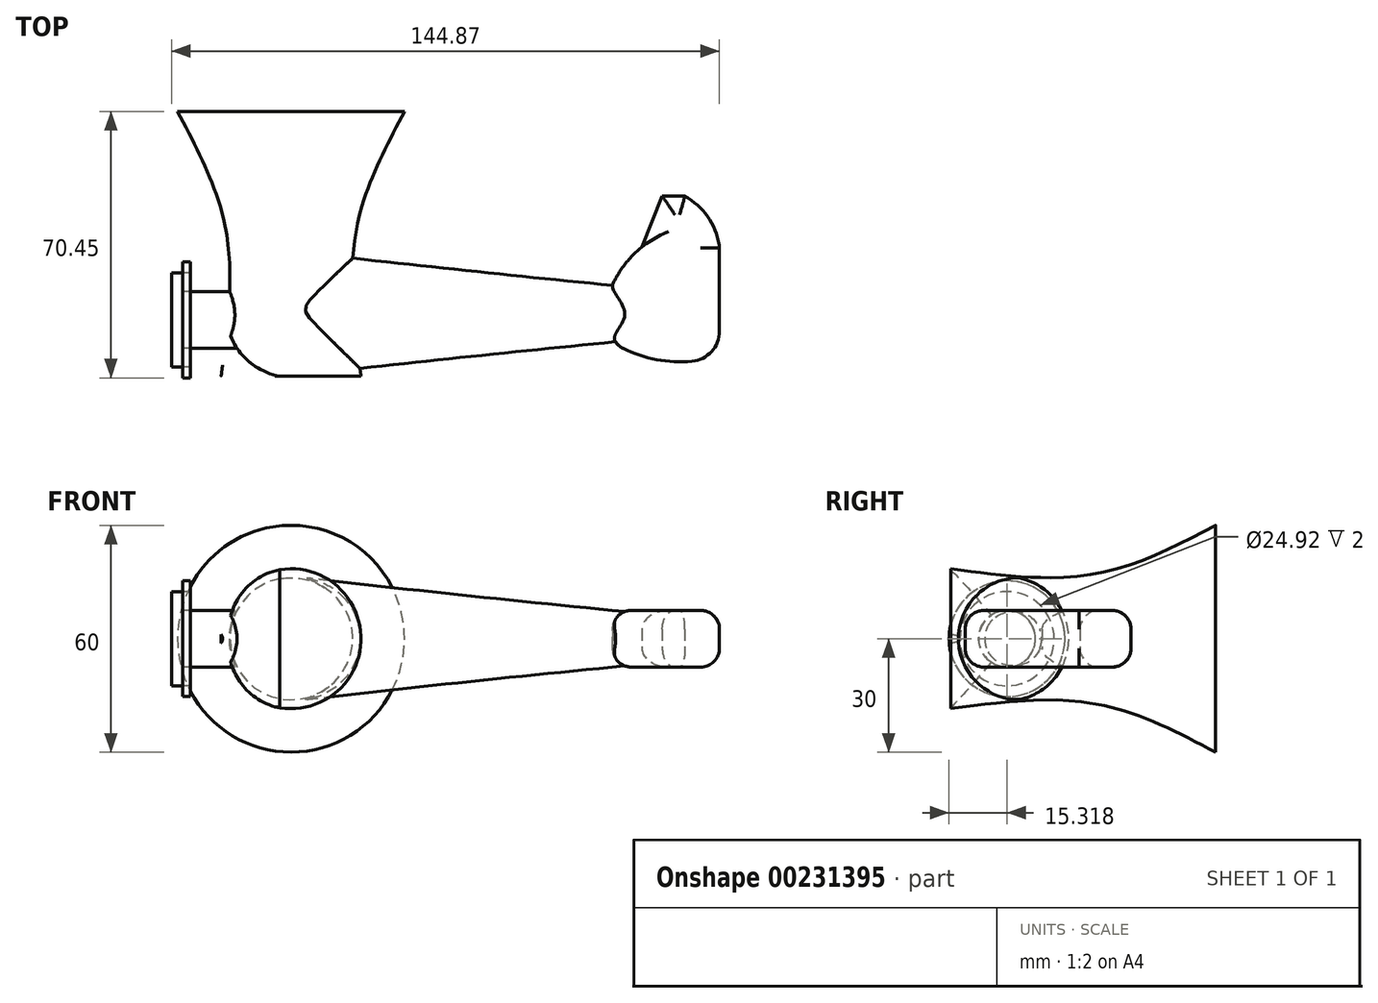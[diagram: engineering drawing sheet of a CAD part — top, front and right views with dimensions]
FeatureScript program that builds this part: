
annotation { "Feature Type Name" : "Feature", "Feature Type Description" : "" }
export const myFeature = defineFeature(function(context is Context, id is Id, definition is map)
    precondition{}
    {
        {
            var Q0;
            Q0=qCreatedBy(makeId("Front.planeOp"),FACE);
            var sketch = newSketch(context, id + "F0", { "sketchPlane" : qUnion([Q0])});
            skCircle(sketch, "E0", {"center": v(0, 0) * mm, "radius": 30 * mm});
            skSolve(sketch);
        }
        {
            var Q0;
            Q0=makeQuery(id+"F0.imprint","IMPRINT",FACE,{"disambiguationData":[TD([[makeQuery(id+"F0.imprint","IMPRINT",EDGE,{"derivedFrom":sQuery(id+"F0.wireOp",EDGE,"E0")}),1.0]])]});
            cPlane(context, id + "F1", {"entities" : qUnion([Q0]), "cplaneType" : CPlaneType.OFFSET, "offset" : 70 * mm, "width" : 150 * mm, "height" : 150 * mm});
        }
        {
            var Q0;
            Q0=qCreatedBy(id+"F1.planeOp",FACE);
            cPlane(context, id + "F2", {"entities" : qUnion([Q0]), "cplaneType" : CPlaneType.OFFSET, "offset" : 40 * mm, "oppositeDirection" : true, "width" : 150 * mm, "height" : 150 * mm});
        }
        {
            var Q0;
            Q0=qCreatedBy(id+"F2.planeOp",FACE);
            var sketch = newSketch(context, id + "F3", { "sketchPlane" : qUnion([Q0])});
            skCircle(sketch, "E1", {"center": v(0, 0) * mm, "radius": 17.5 * mm});
            skSolve(sketch);
        }
        {
            var Q0;
            Q0=qCreatedBy(id+"F1.planeOp",FACE);
            var sketch = newSketch(context, id + "F4", { "sketchPlane" : qUnion([Q0])});
            skCircle(sketch, "E2", {"center": v(0, 0) * mm, "radius": 18.5 * mm});
            skSolve(sketch);
        }
        {
            var Q0;
            Q0=makeQuery(id+"F4.imprint","IMPRINT",FACE,{"disambiguationData":[TD([[makeQuery(id+"F4.imprint","IMPRINT",EDGE,{"derivedFrom":sQuery(id+"F4.wireOp",EDGE,"E2")}),1.0]])]});
            var Q1;
            Q1=makeQuery(id+"F3.imprint","IMPRINT",FACE,{"disambiguationData":[TD([[makeQuery(id+"F3.imprint","IMPRINT",EDGE,{"derivedFrom":sQuery(id+"F3.wireOp",EDGE,"E1")}),1.0]])]});
            var Q2;
            Q2=makeQuery(id+"F0.imprint","IMPRINT",FACE,{"disambiguationData":[TD([[makeQuery(id+"F0.imprint","IMPRINT",EDGE,{"derivedFrom":sQuery(id+"F0.wireOp",EDGE,"E0")}),1.0]])]});
            loft(context, id + "F5", {"sheetProfilesArray" : [{ "sheetProfileEntities" : qUnion([Q0]) }, { "sheetProfileEntities" : qUnion([Q1]) }, { "sheetProfileEntities" : qUnion([Q2]) }]});
        }
        {
            var Q0;
            Q0=qCreatedBy(makeId("Right.planeOp"),FACE);
            cPlane(context, id + "F6", {"entities" : qUnion([Q0]), "cplaneType" : CPlaneType.OFFSET, "offset" : 60 * mm, "width" : 150 * mm, "height" : 150 * mm});
        }
        {
            var Q0;
            Q0=qCreatedBy(id+"F6.planeOp",FACE);
            cPlane(context, id + "F7", {"entities" : qUnion([Q0]), "cplaneType" : CPlaneType.OFFSET, "offset" : 25 * mm, "width" : 150 * mm, "height" : 150 * mm});
        }
        {
            var Q0;
            Q0=qCreatedBy(makeId("Right.planeOp"),FACE);
            var sketch = newSketch(context, id + "F8", { "sketchPlane" : qUnion([Q0])});
            skCircle(sketch, "E3", {"center": v(-53.5, 0) * mm, "radius": 16.5 * mm});
            skSolve(sketch);
        }
        {
            var Q0;
            Q0=qCreatedBy(id+"F6.planeOp",FACE);
            var sketch = newSketch(context, id + "F9", { "sketchPlane" : qUnion([Q0])});
            skCircle(sketch, "E4", {"center": v(-53.5, 0) * mm, "radius": 10 * mm});
            skSolve(sketch);
        }
        {
            var Q0;
            Q0=qCreatedBy(id+"F7.planeOp",FACE);
            var sketch = newSketch(context, id + "F10", { "sketchPlane" : qUnion([Q0])});
            skCircle(sketch, "E5", {"center": v(-53.5, 0) * mm, "radius": 7.5 * mm});
            skSolve(sketch);
        }
        {
            var Q1;
            Q1=qSketchRegion(id+"F8",true);
            var Q2;
            Q2=qSketchRegion(id+"F9",true);
            var Q3;
            Q3=qSketchRegion(id+"F10",true);
            loft(context, id + "F11", {"operationType" : NewBodyOperationType.ADD, "sheetProfilesArray" : [{ "sheetProfileEntities" : qUnion([Q1]) }, { "sheetProfileEntities" : qUnion([Q2]) }, { "sheetProfileEntities" : qUnion([Q3]) }]});
        }
        {
            var Q0;
            Q0=qCreatedBy(makeId("Top.planeOp"),FACE);
            var sketch = newSketch(context, id + "F12", { "sketchPlane" : qUnion([Q0])});
            skArc(sketch, "E6", {"start": v(-2.52, -70.07) * mm, "mid": v(-11.8, -65.57) * mm, "end": v(-16.82, -56.57) * mm});
            skLineSegment(sketch, "E7", {"start": v(-2.52, -70.07) * mm, "end": v(-18.47, -70.07) * mm});
            skLineSegment(sketch, "E8", {"start": v(-18.47, -70.07) * mm, "end": v(-16.82, -56.57) * mm});
            skSolve(sketch);
        }
        {
            var Q0;
            Q0=qCreatedBy(makeId("Top.planeOp"),FACE);
            cPlane(context, id + "F13", {"entities" : qUnion([Q0]), "cplaneType" : CPlaneType.OFFSET, "offset" : 18 * mm, "oppositeDirection" : true, "width" : 150 * mm, "height" : 150 * mm});
        }
        {
            var Q0;
            Q0=qCreatedBy(makeId("Top.planeOp"),FACE);
            var sketch = newSketch(context, id + "F14", { "sketchPlane" : qUnion([Q0])});
            skArc(sketch, "E9.0", {"start": v(-2.52, -70.07) * mm, "mid": v(-11.8, -65.57) * mm, "end": v(-16.82, -56.57) * mm});
            skLineSegment(sketch, "E10.0", {"start": v(-2.52, -70.07) * mm, "end": v(-18.47, -70.07) * mm});
            skLineSegment(sketch, "E11.0", {"start": v(-18.47, -70.07) * mm, "end": v(-16.82, -56.57) * mm});
            skSolve(sketch);
        }
        {
            var Q0;
            Q0=qCreatedBy(id+"F13.planeOp",FACE);
            var sketch = newSketch(context, id + "F15", { "sketchPlane" : qUnion([Q0])});
            skArc(sketch, "E12.0", {"start": v(-2.52, -70.07) * mm, "mid": v(-11.8, -65.57) * mm, "end": v(-16.82, -56.57) * mm});
            skLineSegment(sketch, "E13.0", {"start": v(-2.52, -70.07) * mm, "end": v(-18.47, -70.07) * mm});
            skLineSegment(sketch, "E13.1", {"start": v(-18.47, -70.07) * mm, "end": v(-16.82, -56.57) * mm});
            skSolve(sketch);
        }
        {
            var Q0;
            Q0=qSketchRegion(id+"F15",true);
            extrude(context, id + "F16", {"entities" : qUnion([Q0]), "operationType" : NewBodyOperationType.REMOVE, "endBound" : BoundingType.THROUGH_ALL, "depth" : 25 * mm});
        }
        {
            var Q0;
            Q0=qCreatedBy(makeId("Top.planeOp"),FACE);
            var sketch = newSketch(context, id + "F17", { "sketchPlane" : qUnion([Q0])});
            skLineSegment(sketch, "E14", {"start": v(113.26, -61.15) * mm, "end": v(113.26, -35.74) * mm});
            skLineSegment(sketch, "E15", {"start": v(98.14, -22.36) * mm, "end": v(92.74, -35.88) * mm});
            skArc(sketch, "E16", {"start": v(113.26, -64.6) * mm, "mid": v(98.75, -65.96) * mm, "end": v(85, -61.15) * mm});
            skLineSegment(sketch, "E17", {"start": v(113.26, -64.6) * mm, "end": v(113.26, -61.15) * mm});
            skArc(sketch, "E18", {"start": v(113.26, -35.74) * mm, "mid": v(110.25, -27.99) * mm, "end": v(104.12, -22.36) * mm});
            skLineSegment(sketch, "E19", {"start": v(98.14, -22.36) * mm, "end": v(104.12, -22.36) * mm});
            skArc(sketch, "E20", {"start": v(92.74, -35.88) * mm, "mid": v(88.28, -40.4) * mm, "end": v(85, -45.84) * mm});
            skLineSegment(sketch, "E21", {"start": v(85, -61.15) * mm, "end": v(85, -45.84) * mm});
            skSolve(sketch);
        }
        {
            var Q0;
            Q0=qSketchRegion(id+"F17",true);
            extrude(context, id + "F18", {"entities" : qUnion([Q0]), "operationType" : NewBodyOperationType.ADD, "endBound" : BoundingType.SYMMETRIC, "depth" : 15 * mm});
        }
        {
            var Q0;
            Q0=makeQuery(id+"F18.opExtrude","SWEPT_EDGE",EDGE,{"disambiguationData":[OSD([sQuery(id+"F17.wireOp",EDGE,"E16"),sQuery(id+"F17.wireOp",EDGE,"E17")])]});
            fillet(context, id + "F19", {"entities" : qUnion([Q0]), "radius" : 8 * mm, "tangentPropagation" : true, "allowEdgeOverflow" : false});
        }
        {
            var Q0;
            {var subQ0=sQuery(id+"F17.wireOp",EDGE,"E21");var subQ1=sQuery(id+"F17.wireOp",EDGE,"E16");Q0=makeQuery(id+"F18.boolean.opBoolean","SPLIT",EDGE,{"disambiguationData":[TD([makeQuery(id+"F18.opExtrude","SWEPT_FACE",FACE,{"disambiguationData":[OSD([subQ1])]})])],"derivedFrom":makeQuery(id+"F18.opExtrude","CAP_EDGE",EDGE,{"disambiguationData":[OSD([subQ0])],"isStart":true})});}
            var Q1;
            {var subQ0=sQuery(id+"F17.wireOp",EDGE,"E21");var subQ1=sQuery(id+"F17.wireOp",EDGE,"E20");Q1=makeQuery(id+"F18.boolean.opBoolean","SPLIT",EDGE,{"disambiguationData":[TD([makeQuery(id+"F18.opExtrude","SWEPT_FACE",FACE,{"disambiguationData":[OSD([subQ1])]})])],"derivedFrom":makeQuery(id+"F18.opExtrude","CAP_EDGE",EDGE,{"disambiguationData":[OSD([subQ0])],"isStart":true})});}
            var Q2;
            Q2=makeQuery(id+"F18.opExtrude","SWEPT_EDGE",EDGE,{"disambiguationData":[OSD([sQuery(id+"F17.wireOp",EDGE,"E16"),sQuery(id+"F17.wireOp",EDGE,"E21")])]});
            fillet(context, id + "F20", {"entities" : qUnion([Q0, Q1, Q2]), "radius" : 5 * mm, "tangentPropagation" : true, "allowEdgeOverflow" : false});
        }
        {
            var Q0;
            Q0=makeQuery(id+"F18.opExtrude","CAP_EDGE",EDGE,{"disambiguationData":[OSD([sQuery(id+"F17.wireOp",EDGE,"E16")])],"isStart":true});
            fillet(context, id + "F21", {"entities" : qUnion([Q0]), "radius" : 5 * mm, "tangentPropagation" : true, "allowEdgeOverflow" : false});
        }
        {
            var Q0;
            Q0=makeQuery(id+"F18.opExtrude","CAP_EDGE",EDGE,{"disambiguationData":[OSD([sQuery(id+"F17.wireOp",EDGE,"E16")])],"isStart":false});
            var Q1;
            {var subQ0=sQuery(id+"F17.wireOp",EDGE,"E21");var subQ1=sQuery(id+"F17.wireOp",EDGE,"E20");Q1=makeQuery(id+"F18.boolean.opBoolean","SPLIT",EDGE,{"disambiguationData":[TD([makeQuery(id+"F18.opExtrude","SWEPT_FACE",FACE,{"disambiguationData":[OSD([subQ1])]})])],"derivedFrom":makeQuery(id+"F18.opExtrude","CAP_EDGE",EDGE,{"disambiguationData":[OSD([subQ0])],"isStart":false})});}
            var Q2;
            Q2=makeQuery(id+"F18.opExtrude","CAP_EDGE",EDGE,{"disambiguationData":[OSD([sQuery(id+"F17.wireOp",EDGE,"E15")])],"isStart":false});
            var Q3;
            Q3=makeQuery(id+"F18.opExtrude","CAP_EDGE",EDGE,{"disambiguationData":[OSD([sQuery(id+"F17.wireOp",EDGE,"E19")])],"isStart":false});
            fillet(context, id + "F22", {"entities" : qUnion([Q0, Q1, Q2, Q3]), "radius" : 5 * mm, "tangentPropagation" : true, "allowEdgeOverflow" : false});
        }
        {
            var Q0;
            Q0=makeQuery(id+"F18.opExtrude","CAP_EDGE",EDGE,{"disambiguationData":[OSD([sQuery(id+"F17.wireOp",EDGE,"E19")])],"isStart":true});
            var Q1;
            Q1=makeQuery(id+"F18.opExtrude","CAP_EDGE",EDGE,{"disambiguationData":[OSD([sQuery(id+"F17.wireOp",EDGE,"E18")])],"isStart":true});
            var Q2;
            Q2=makeQuery(id+"F21.opFillet","BLEND_EDGE",EDGE,{"blendedFrom":[makeQuery(id+"F18.opExtrude","CAP_EDGE",EDGE,{"disambiguationData":[OSD([sQuery(id+"F17.wireOp",EDGE,"E14"),sQuery(id+"F17.wireOp",EDGE,"E17")])],"isStart":true}),makeQuery(id+"F18.opExtrude","SWEPT_FACE",FACE,{"disambiguationData":[OSD([sQuery(id+"F17.wireOp",EDGE,"E18")])]})],"blendedInto":[makeQuery(id+"F18.opExtrude","SWEPT_FACE",FACE,{"disambiguationData":[OSD([sQuery(id+"F17.wireOp",EDGE,"E18")])]})]});
            var Q3;
            Q3=makeQuery(id+"F18.opExtrude","CAP_EDGE",EDGE,{"disambiguationData":[OSD([sQuery(id+"F17.wireOp",EDGE,"E15")])],"isStart":true});
            fillet(context, id + "F23", {"entities" : qUnion([Q0, Q1, Q2, Q3]), "radius" : 5 * mm, "tangentPropagation" : true, "allowEdgeOverflow" : false});
        }
        {
            var Q0;
            Q0=qCreatedBy(makeId("Top.planeOp"),FACE);
            var sketch = newSketch(context, id + "F24", { "sketchPlane" : qUnion([Q0])});
            skLineSegment(sketch, "E22", {"start": v(-13.96, -62.63) * mm, "end": v(-28.6, -62.63) * mm});
            skLineSegment(sketch, "E23", {"start": v(-28.6, -62.63) * mm, "end": v(-28.6, -47.64) * mm});
            skLineSegment(sketch, "E24", {"start": v(-28.6, -47.64) * mm, "end": v(-13.96, -47.64) * mm});
            skLineSegment(sketch, "E25", {"start": v(-13.96, -47.64) * mm, "end": v(-13.96, -62.63) * mm});
            skLineSegment(sketch, "E26", {"start": v(-28.6, -55.13) * mm, "end": v(-13.96, -55.13) * mm});
            skSolve(sketch);
        }
        {
            var Q0;
            {var subQ0=sQuery(id+"F24.wireOp",EDGE,"E22");Q0=makeQuery(id+"F24.imprint","IMPRINT",FACE,{"disambiguationData":[TD([[makeQuery(id+"F24.imprint","IMPRINT",EDGE,{"derivedFrom":subQ0}),-1.0]])]});}
            var Q1;
            Q1=sQuery(id+"F24.wireOp",EDGE,"E26");
            revolve(context, id + "F25", {"operationType" : NewBodyOperationType.ADD, "entities" : qUnion([Q0]), "axis" : qUnion([Q1]), "revolveType" : RevolveType.FULL});
        }
        {
            var Q0;
            Q0=makeQuery(id+"F25.opRevolve","SWEPT_FACE",FACE,{"disambiguationData":[OSD([sQuery(id+"F24.wireOp",EDGE,"E23")])]});
            var sketch = newSketch(context, id + "F26", { "sketchPlane" : qUnion([Q0])});
            skCircle(sketch, "E27", {"center": v(55.13, 0) * mm, "radius": 15.32 * mm});
            skCircle(sketch, "E28", {"center": v(55.13, 0) * mm, "radius": 12.46 * mm});
            skSolve(sketch);
        }
        {
            var Q0;
            Q0=makeQuery(id+"F26.imprint","IMPRINT",FACE,{"disambiguationData":[TD([[makeQuery(id+"F26.imprint","IMPRINT",EDGE,{"derivedFrom":sQuery(id+"F26.wireOp",EDGE,"E28")}),1.0]])]});
            extrude(context, id + "F27", {"entities" : qUnion([Q0]), "depth" : 3 * mm});
        }
        {
            var Q0;
            Q0=makeQuery(id+"F26.imprint","IMPRINT",FACE,{"disambiguationData":[TD([[makeQuery(id+"F26.imprint","IMPRINT",EDGE,{"derivedFrom":sQuery(id+"F26.wireOp",EDGE,"E27")}),1.0]])]});
            extrude(context, id + "F28", {"entities" : qUnion([Q0]), "oppositeDirection" : true, "depth" : 2 * mm});
        }
        {
            var Q0;
            Q0=makeQuery(id+"F26.imprint","IMPRINT",FACE,{"disambiguationData":[TD([[makeQuery(id+"F26.imprint","IMPRINT",EDGE,{"derivedFrom":makeQuery(id+"F25.opRevolve","SWEPT_EDGE",EDGE,{"disambiguationData":[OSD([sQuery(id+"F24.wireOp",EDGE,"E22"),sQuery(id+"F24.wireOp",EDGE,"E23")])]})}),1.0]])]});
            extrude(context, id + "F29", {"entities" : qUnion([Q0]), "operationType" : NewBodyOperationType.ADD, "depth" : 3 * mm});
        }
    });
